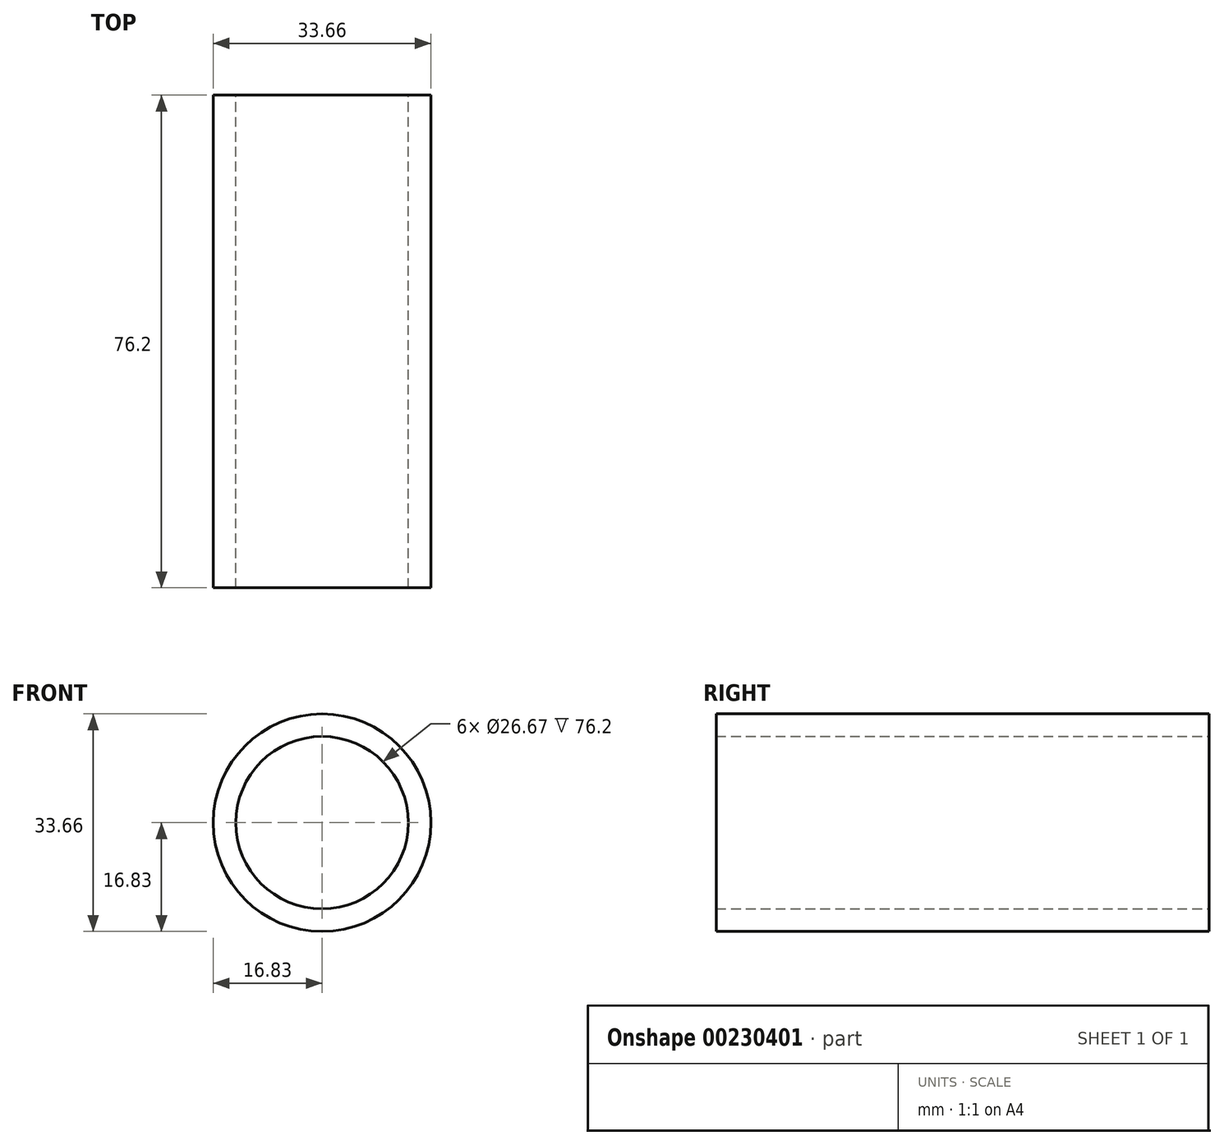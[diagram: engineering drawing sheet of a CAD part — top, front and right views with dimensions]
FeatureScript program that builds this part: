
annotation { "Feature Type Name" : "Feature", "Feature Type Description" : "" }
export const myFeature = defineFeature(function(context is Context, id is Id, definition is map)
    precondition{}
    {
        {
            var Q0;
            Q0=qCreatedBy(makeId("Front.planeOp"),FACE);
            var sketch = newSketch(context, id + "F0", { "sketchPlane" : qUnion([Q0])});
            skCircle(sketch, "E0", {"center": v(0, 0) * mm, "radius": 13.34 * mm});
            skCircle(sketch, "E1", {"center": v(0, 0) * mm, "radius": 16.83 * mm});
            skSolve(sketch);
        }
        {
            var Q0;
            Q0=qSketchRegion(id+"F0",true);
            extrude(context, id + "F1", {"entities" : qUnion([Q0]), "depth" : 76.2 * mm});
        }
    });
